# Revit family: REX_2_22W_3000K_2400LM
name_source: partatom
category: Lighting Fixtures
units: mm (PartAtom-declared; Revit-internal decimal feet)

## family parameters
Always vertical = Yes
Cut with Voids When Loaded = No
Host = Ceiling
Light Source = Yes
OmniClass Number = 23.80.70.11
OmniClass Title = Luminaries for Internal Lighting
Part Type = Normal
Room Calculation Point = No
Round Connector Dimension = Use Diameter
Shared = No

## types (1)
- Type 1
    Alimentation luminaire = AC 220-240V
    Angle d'éclairage = 45°
    Color Filter = 16777215
    Default Elevation = 0 mm  [stored 0 ft]
    Dimensions = Ø 115 mm, H = 160 mm
    Dimming Lamp Color Temperature Shift = <None>
    Driver = Driver Lifud TUV CE RCM CCC
    Durée de vie = 50 000 heures
    Fintion = Blanc et réflecteur chrome
    IRC = >90
    Maintien du flux = L80B10 (50 000 heures)
    Matériau = Acier
    Photometric Web File = google_eulumdat_converter (25).ies
    Puissance nominale = 22,5W
    SDCM = 3
    Tilt Angle = 90.00°
    Type = Downlight
    Type de lampe = LED XC18-COB Bridgelux 2630

note: [stored X ft] marks values corroborated as IEEE doubles in the binary element streams (Revit-internal decimal feet)

## geometry (parser evidence)
native form markers: Sweep x3
no freeform markers — native parametric forms only
